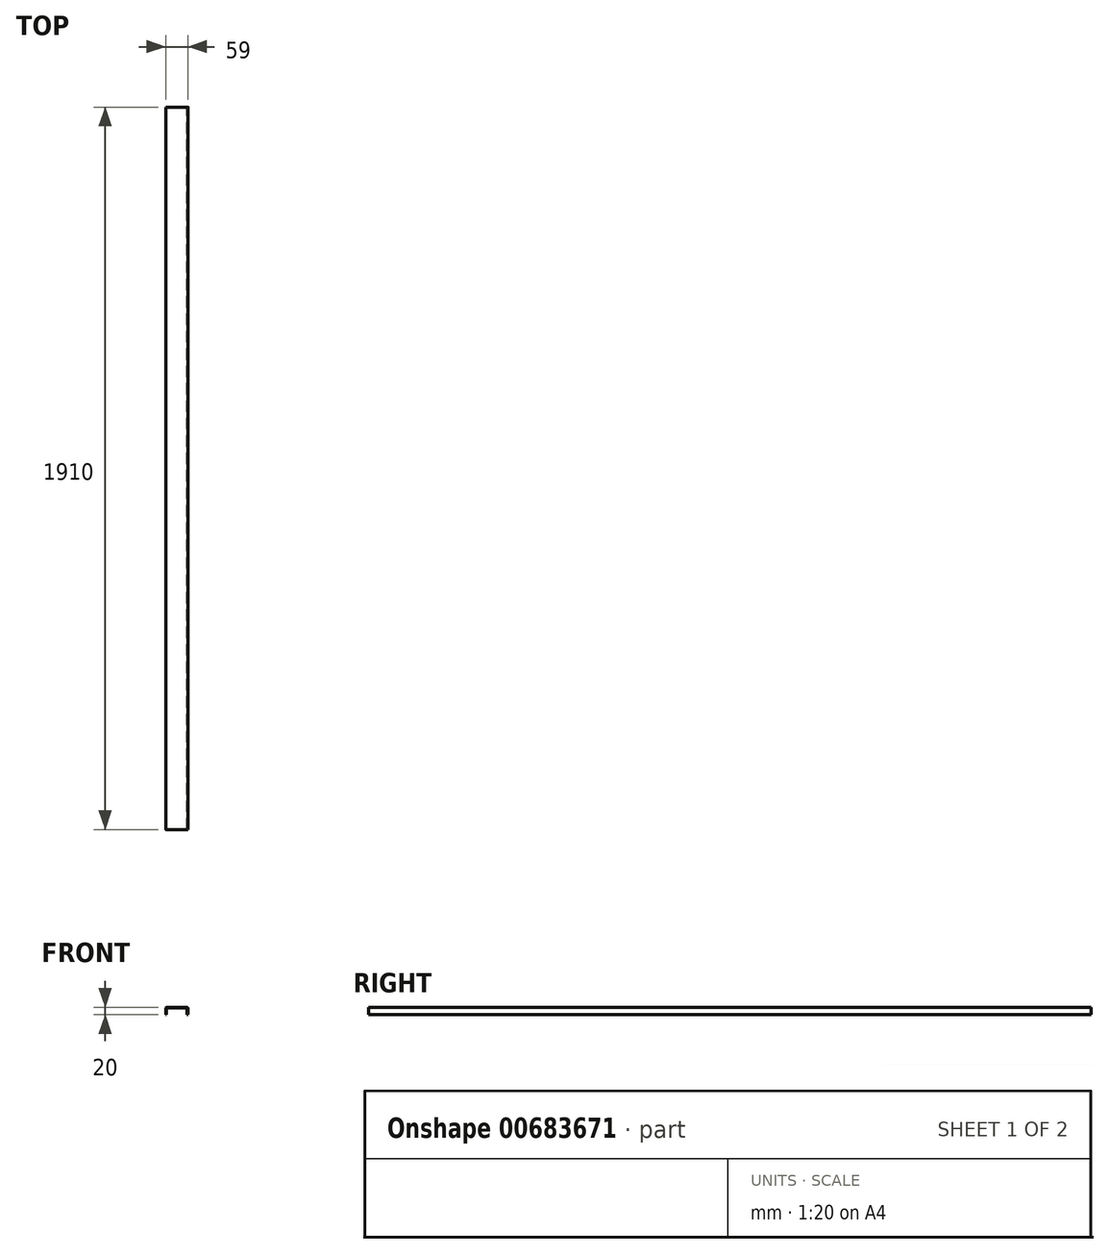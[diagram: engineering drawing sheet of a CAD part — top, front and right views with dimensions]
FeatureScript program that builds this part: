
annotation { "Feature Type Name" : "Feature", "Feature Type Description" : "" }
export const myFeature = defineFeature(function(context is Context, id is Id, definition is map)
    precondition{}
    {
        {
            var Q0;
            Q0=qCreatedBy(makeId("Front.planeOp"),FACE);
            var sketch = newSketch(context, id + "F0", { "sketchPlane" : qUnion([Q0])});
            skLineSegment(sketch, "E0.bottom", {"start": v(0, 0) * mm, "end": v(2, 0) * mm});
            skLineSegment(sketch, "E0.top", {"start": v(4, 20) * mm, "end": v(55, 20) * mm});
            skLineSegment(sketch, "E0.left", {"start": v(0, 0) * mm, "end": v(0, 16) * mm});
            skLineSegment(sketch, "E0.right", {"start": v(59, 0) * mm, "end": v(59, 16) * mm});
            skLineSegment(sketch, "E1.0", {"start": v(2, 0) * mm, "end": v(2, 16) * mm});
            skLineSegment(sketch, "E2.0", {"start": v(57, 0) * mm, "end": v(57, 16) * mm});
            skLineSegment(sketch, "E2.1", {"start": v(4, 18) * mm, "end": v(55, 18) * mm});
            skLineSegment(sketch, "E3.trimOffspring", {"start": v(57, 0) * mm, "end": v(59, 0) * mm});
            skArc(sketch, "E4.filletArc", {"start": v(4, 18) * mm, "mid": v(2.59, 17.41) * mm, "end": v(2, 16) * mm});
            skPoint(sketch, "E5.visualSharp", {"position": v(57, 18) * mm});
            skArc(sketch, "E5.filletArc", {"start": v(57, 16) * mm, "mid": v(56.41, 17.41) * mm, "end": v(55, 18) * mm});
            skPoint(sketch, "E6.visualSharp", {"position": v(0, 20) * mm});
            skArc(sketch, "E6.filletArc", {"start": v(4, 20) * mm, "mid": v(1.17, 18.83) * mm, "end": v(0, 16) * mm});
            skPoint(sketch, "E7.visualSharp", {"position": v(59, 20) * mm});
            skArc(sketch, "E7.filletArc", {"start": v(59, 16) * mm, "mid": v(57.83, 18.83) * mm, "end": v(55, 20) * mm});
            skSolve(sketch);
        }
        {
            var Q0;
            Q0=makeQuery(id+"F0.imprint","IMPRINT",FACE,{"disambiguationData":[TD([[makeQuery(id+"F0.imprint","IMPRINT",EDGE,{"derivedFrom":sQuery(id+"F0.wireOp",EDGE,"E0.bottom")}),1.0]])]});
            extrude(context, id + "F1", {"entities" : qUnion([Q0]), "depth" : 1910 * mm, "offsetDistance" : 25 * mm});
        }
    });
